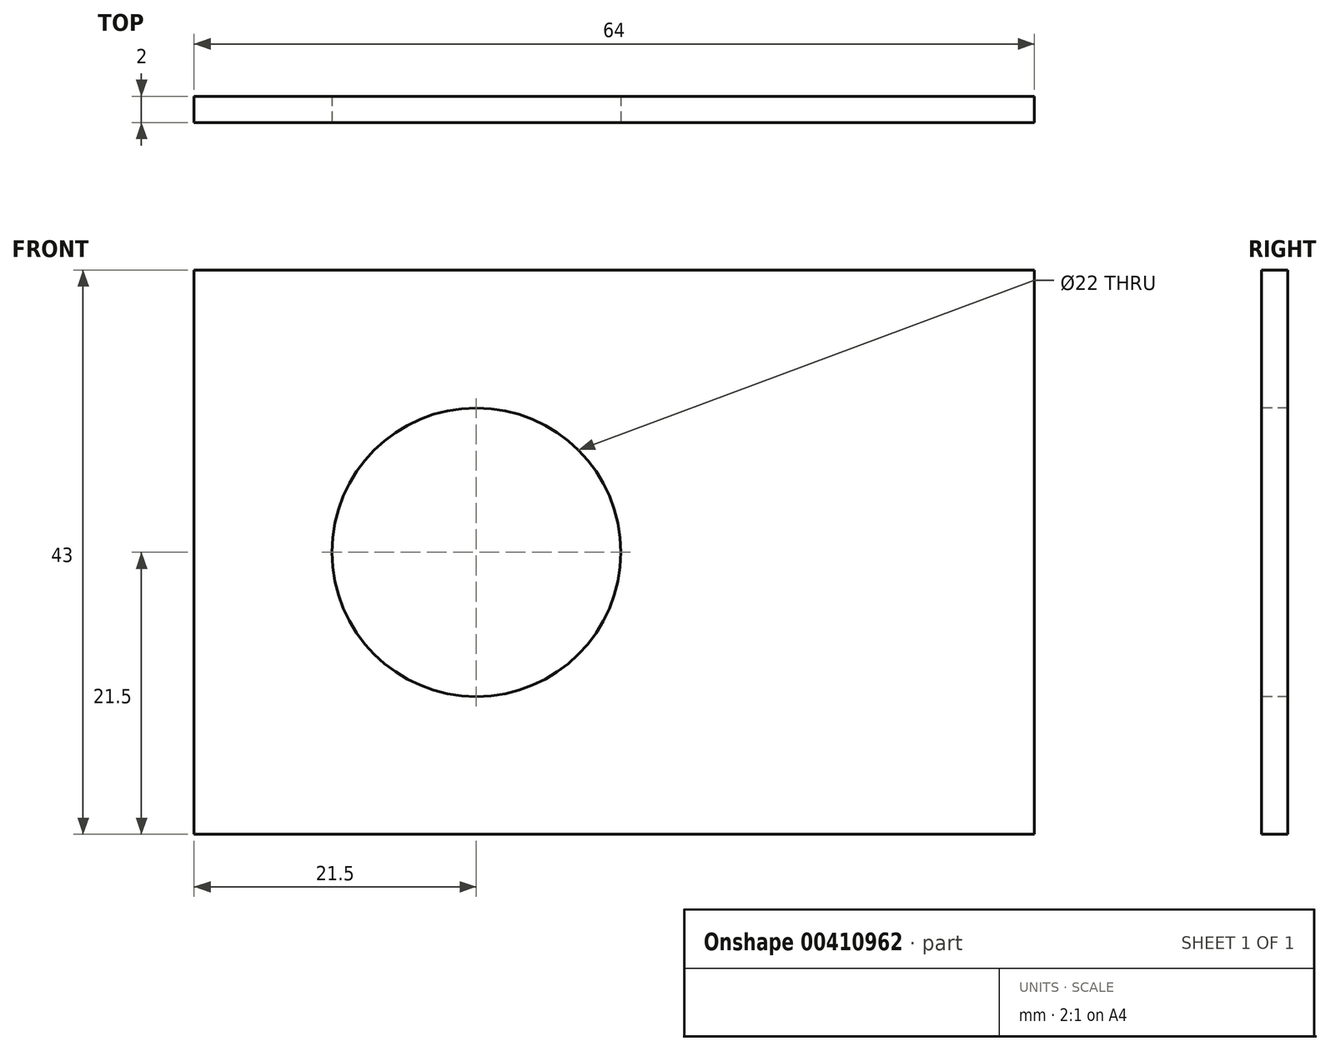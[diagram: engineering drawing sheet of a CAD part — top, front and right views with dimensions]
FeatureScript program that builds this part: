
annotation { "Feature Type Name" : "Feature", "Feature Type Description" : "" }
export const myFeature = defineFeature(function(context is Context, id is Id, definition is map)
    precondition{}
    {
        {
            var Q0;
            Q0=qCreatedBy(makeId("Front.planeOp"),FACE);
            var sketch = newSketch(context, id + "F0", { "sketchPlane" : qUnion([Q0])});
            skLineSegment(sketch, "E0", {"start": v(0, 0) * mm, "end": v(64, 0) * mm});
            skLineSegment(sketch, "E1", {"start": v(64, 0) * mm, "end": v(64, -43) * mm});
            skLineSegment(sketch, "E2", {"start": v(64, -43) * mm, "end": v(0, -43) * mm});
            skLineSegment(sketch, "E3", {"start": v(0, -43) * mm, "end": v(0, 0) * mm});
            skLineSegment(sketch, "E4", {"start": v(0, 0) * mm, "end": v(43, 0) * mm});
            skCircle(sketch, "E5", {"center": v(21.5, -21.5) * mm, "radius": 11 * mm});
            skSolve(sketch);
        }
        {
            var Q0;
            Q0=makeQuery(id+"F0.imprint","IMPRINT",FACE,{"disambiguationData":[TD([[makeQuery(id+"F0.imprint","IMPRINT",EDGE,{"derivedFrom":sQuery(id+"F0.wireOp",EDGE,"E0")}),-1.0]])]});
            extrude(context, id + "F1", {"entities" : qUnion([Q0]), "depth" : -2 * mm});
        }
    });
